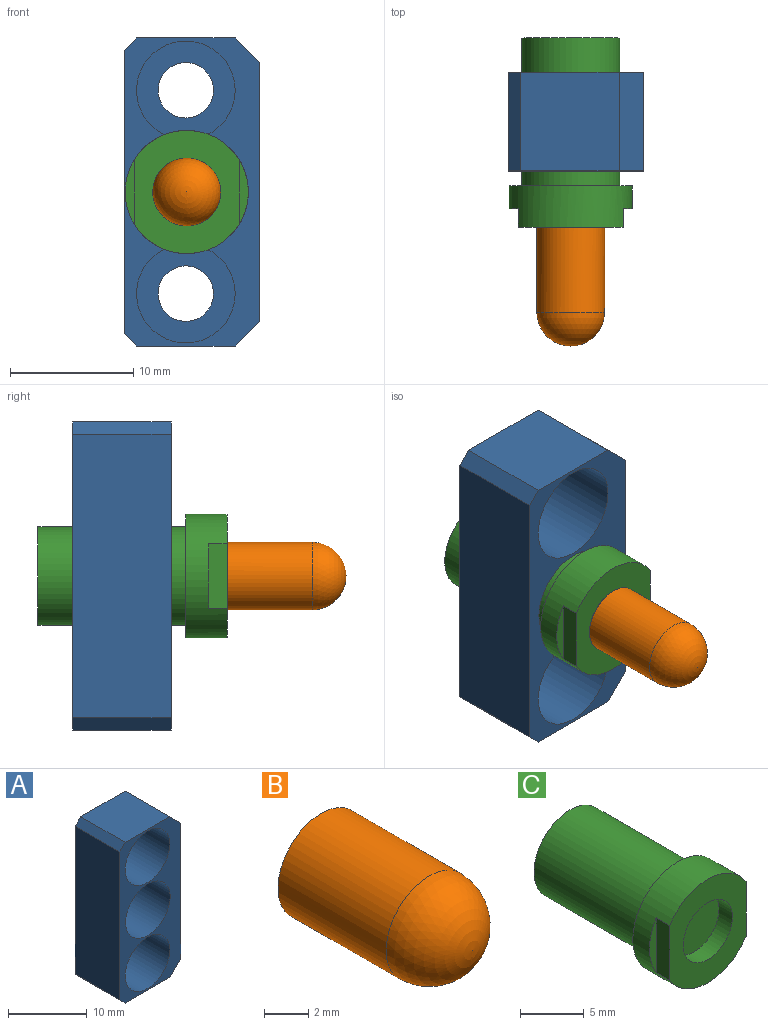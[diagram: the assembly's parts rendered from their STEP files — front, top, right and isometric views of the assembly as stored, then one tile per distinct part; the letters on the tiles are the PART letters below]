
ASSEMBLY  parts=3 mates=3
PART A: 17 faces, bbox 11x8x25 mm
  f0: plane 25x11mm, normal (0,-1,0), area 119.2mm2, adj f2,f3,f6,f7,f8,f9,f10,f12
  f1: plane 25x11mm, normal (0,1,0), area 187.9mm2, adj f2,f3,f4,f5,f6,f7,f8,f9
  f2: plane 8x1mm, normal (-0.71,0,0.71), area 11.3mm2, adj f0,f1,f8,f16
  f3: plane 8x1mm, normal (-0.71,0,-0.71), area 11.3mm2, adj f0,f1,f6,f16
  f4: cylinder r=2.25mm len=4.5mm, axis (0,-1,0), area 14.1mm2, adj f1,f13
  f5: cylinder r=2.25mm len=4.5mm, axis (0,-1,0), area 14.1mm2, adj f1,f11
  f6: plane 8x8mm, normal (0,0,-1), area 64mm2, adj f0,f1,f3,f9
  f7: plane 21x8mm, normal (1,0,0), area 168mm2, adj f0,f1,f9,f10
  f8: plane 8x8mm, normal (0,0,1), area 64mm2, adj f0,f1,f2,f10
  f9: plane 8x2mm, normal (0.71,0,-0.71), area 22.6mm2, adj f0,f1,f6,f7
  f10: plane 8x2mm, normal (0.71,0,0.71), area 22.6mm2, adj f0,f1,f7,f8
  f11: plane 8x8mm, normal (0,-1,0), area 34.4mm2, adj f5,f12
  f12: cylinder r=4mm len=8mm, axis (0,-1,0), area 175.9mm2, adj f0,f11
  f13: plane 8x8mm, normal (0,-1,0), area 34.4mm2, adj f4,f14
  f14: cylinder r=4mm len=8mm, axis (0,-1,0), area 175.9mm2, adj f0,f13
  f15: cylinder r=4mm len=8mm, axis (0,1,0), area 201.1mm2, adj f0,f1
  f16: plane 23x8mm, normal (-1,0,0), area 184mm2, adj f0,f1,f2,f3
PART B: 3 faces, bbox 5.5x9.7x5.5 mm
  f0: sphere r=2.75mm, area 47.5mm2, adj f1
  f1: cylinder r=2.75mm len=6.9mm, axis (0,-1,0), area 119.2mm2, adj f0,f2
  f2: plane 5.5x5.5mm, normal (0,1,0), area 23.8mm2, adj f1
PART C: 11 faces, bbox 10x15.4x10 mm
  f0: plane 10x8.5mm, normal (0,-1,0), area 49.4mm2, adj f1,f2,f4,f6
  f1: cylinder r=5mm len=10mm, axis (0,1,0), area 88.6mm2, adj f0,f4,f5,f6,f7,f9
  f2: cylinder r=2.75mm len=5.5mm, axis (0,-1,0), area 25.9mm2, adj f0,f3
  f3: plane 5.5x5.5mm, normal (0,-1,0), area 23.8mm2, adj f2
  f4: plane 5.27x1.5mm, normal (1,0,0), area 7.9mm2, adj f0,f1,f5
  f5: plane 5.27x0.75mm, normal (0,-1,0), area 2.7mm2, adj f1,f4
  f6: plane 5.27x1.5mm, normal (-1,0,0), area 7.9mm2, adj f0,f1,f7
  f7: plane 5.27x0.75mm, normal (0,-1,0), area 2.7mm2, adj f1,f6
  f8: cylinder r=4mm len=12mm, axis (0,1,0), area 301.6mm2, adj f9,f10
  f9: plane 10x10mm, normal (0,1,0), area 28.3mm2, adj f1,f8
  f10: plane 8x8mm, normal (0,1,0), area 50.3mm2, adj f8
PLACE A t=(-19.24,0.26,-2.41)mm
PLACE B t=(-17.35,3.07,0.86)mm
PLACE C t=(-17.35,3.07,0.86)mm
MATE cylindrical B.f1 <-> C.f1  axis (0,-1,0) through (-17.35,-15.73,0.86)mm
MATE planar B.f1 <-> C.f1  axis (0,1,0) through (-17.35,-12.28,0.86)mm
MATE cylindrical C.f1 <-> A.f15  axis (0,1,0) through (-17.35,-2.93,0.86)mm
